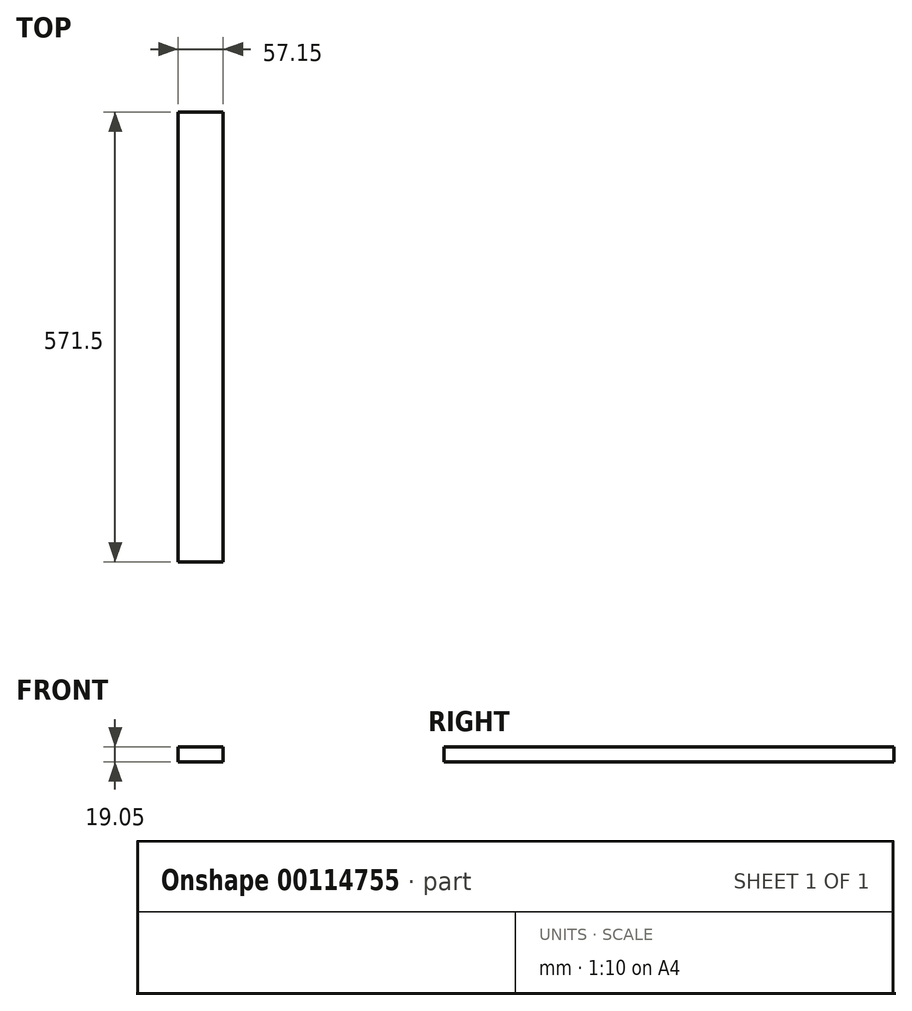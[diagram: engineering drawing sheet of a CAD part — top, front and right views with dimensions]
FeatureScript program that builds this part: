
annotation { "Feature Type Name" : "Feature", "Feature Type Description" : "" }
export const myFeature = defineFeature(function(context is Context, id is Id, definition is map)
    precondition{}
    {
        {
            var Q0;
            Q0=qCreatedBy(makeId("Top.planeOp"),FACE);
            var sketch = newSketch(context, id + "F0", { "sketchPlane" : qUnion([Q0])});
            skLineSegment(sketch, "E0.bottom", {"start": v(0, 0) * mm, "end": v(57.15, 0) * mm});
            skLineSegment(sketch, "E0.top", {"start": v(0, 571.5) * mm, "end": v(57.15, 571.5) * mm});
            skLineSegment(sketch, "E0.left", {"start": v(0, 0) * mm, "end": v(0, 571.5) * mm});
            skLineSegment(sketch, "E0.right", {"start": v(57.15, 0) * mm, "end": v(57.15, 571.5) * mm});
            skSolve(sketch);
        }
        {
            var Q0;
            Q0=qSketchRegion(id+"F0",true);
            extrude(context, id + "F1", {"entities" : qUnion([Q0]), "depth" : 19.05 * mm});
        }
    });
